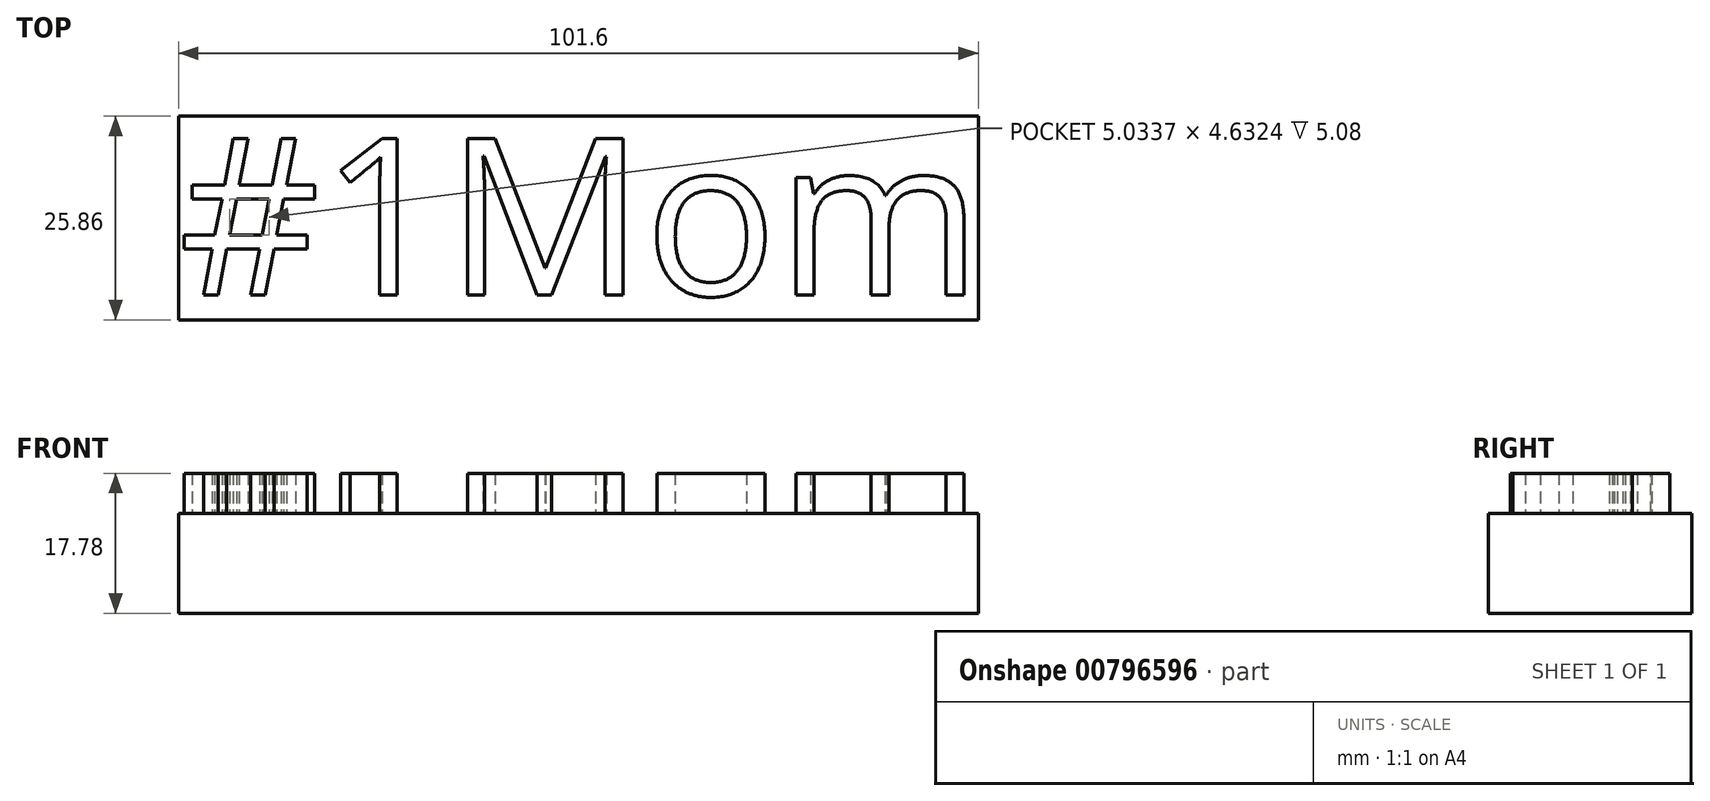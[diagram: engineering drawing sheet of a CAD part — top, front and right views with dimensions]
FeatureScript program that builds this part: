
annotation { "Feature Type Name" : "Feature", "Feature Type Description" : "" }
export const myFeature = defineFeature(function(context is Context, id is Id, definition is map)
    precondition{}
    {
        {
            var Q0;
            Q0=qCreatedBy(makeId("Top.planeOp"),FACE);
            var sketch = newSketch(context, id + "F0", { "sketchPlane" : qUnion([Q0])});
            skText(sketch, "E0", { "text": "#1Mom", "fontName": "OpenSans-Regular.ttf"});
            const initialGuessF0  = {"E0": [0, -0.0201, 1, 0, 0.0201]};
            skSetInitialGuess(sketch, initialGuessF0);
            skSolve(sketch);
        }
        {
            var Q0;
            Q0=qCreatedBy(makeId("Top.planeOp"),FACE);
            var sketch = newSketch(context, id + "F1", { "sketchPlane" : qUnion([Q0])});
            skLineSegment(sketch, "E1.bottom", {"start": v(101.6, 2.64) * mm, "end": v(0, 2.64) * mm});
            skLineSegment(sketch, "E1.top", {"start": v(101.6, -23.22) * mm, "end": v(0, -23.22) * mm});
            skLineSegment(sketch, "E1.left", {"start": v(101.6, 2.64) * mm, "end": v(101.6, -23.22) * mm});
            skLineSegment(sketch, "E1.right", {"start": v(0, 2.64) * mm, "end": v(0, -23.22) * mm});
            skPoint(sketch, "E1.middle", {"position": v(50.8, -10.3) * mm});
            skSolve(sketch);
        }
        {
            var Q0;
            Q0=makeQuery(id+"F1.imprint","IMPRINT",FACE,{"disambiguationData":[TD([[makeQuery(id+"F1.imprint","IMPRINT",EDGE,{"derivedFrom":sQuery(id+"F1.wireOp",EDGE,"E1.bottom")}),1.0]])]});
            extrude(context, id + "F2", {"entities" : qUnion([Q0]), "oppositeDirection" : true, "depth" : 12.7 * mm, "offsetDistance" : 25.4 * mm});
        }
        {
            var Q0;
            Q0 = qSketchRegion(id + "F0", true);
            extrude(context, id + "F3", {"entities" : qUnion([Q0]), "operationType" : NewBodyOperationType.ADD, "depth" : 5.08 * mm, "offsetDistance" : 25.4 * mm});
        }
    });
